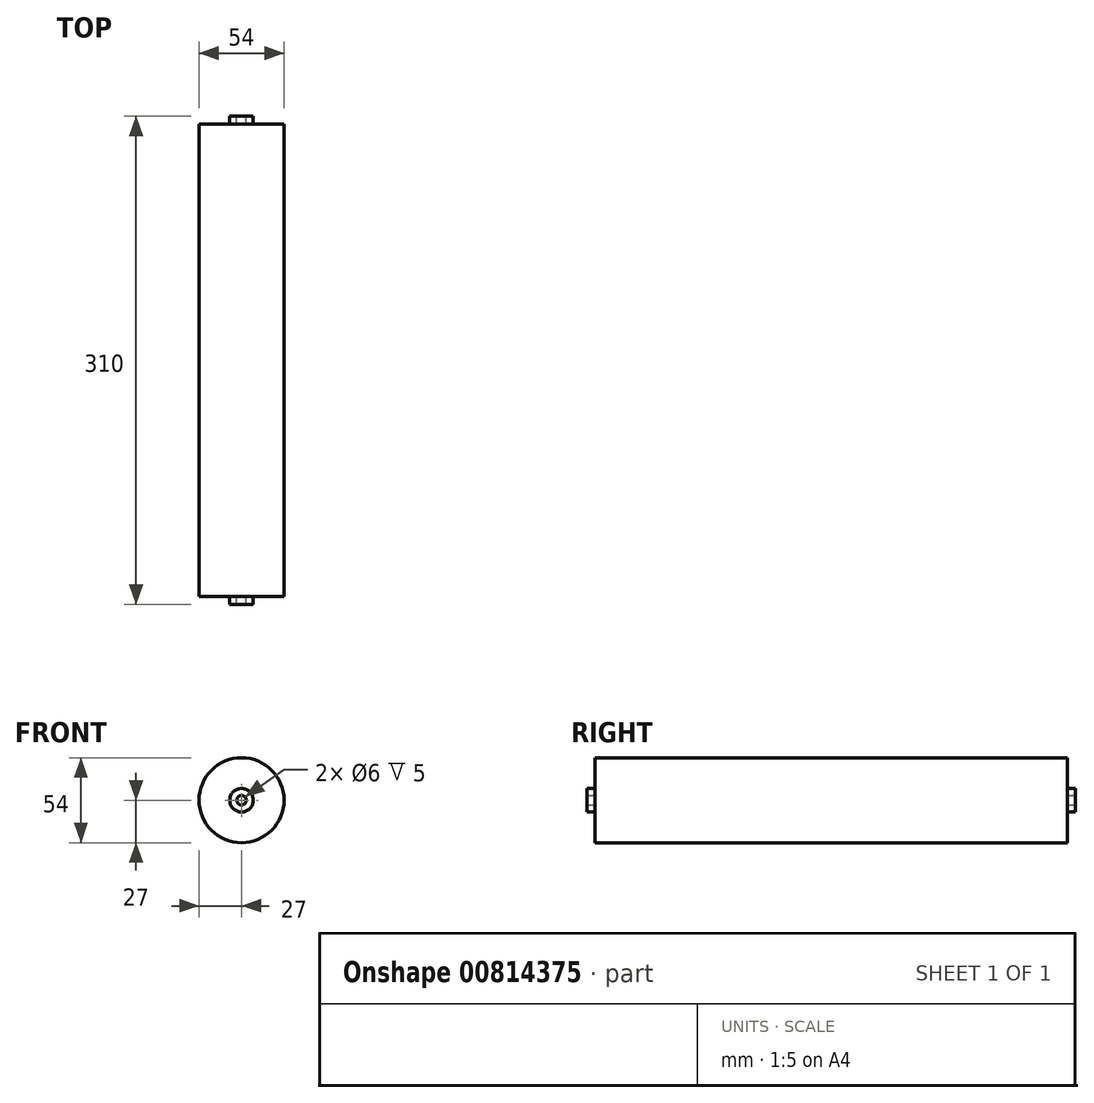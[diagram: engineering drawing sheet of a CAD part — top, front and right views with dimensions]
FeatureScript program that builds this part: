
annotation { "Feature Type Name" : "Feature", "Feature Type Description" : "" }
export const myFeature = defineFeature(function(context is Context, id is Id, definition is map)
    precondition{}
    {
        {
            var Q0;
            Q0=qCreatedBy(makeId("Front.planeOp"),FACE);
            var sketch = newSketch(context, id + "F0", { "sketchPlane" : qUnion([Q0])});
            skCircle(sketch, "E0", {"center": v(0, 0) * mm, "radius": 27 * mm});
            skCircle(sketch, "E1", {"center": v(0, 0) * mm, "radius": 3 * mm});
            skCircle(sketch, "E2", {"center": v(0, 0) * mm, "radius": 7.48 * mm});
            skSolve(sketch);
        }
        {
            var Q0;
            Q0=makeQuery(id+"F0.imprint","IMPRINT",FACE,{"disambiguationData":[TD([[makeQuery(id+"F0.imprint","IMPRINT",EDGE,{"derivedFrom":sQuery(id+"F0.wireOp",EDGE,"E1")}),1.0]])]});
            extrude(context, id + "F1", {"entities" : qUnion([Q0]), "depth" : 300 * mm, "offsetDistance" : 25 * mm, "symmetric" : true});
        }
        {
            var Q0;
            Q0=makeQuery(id+"F0.imprint","IMPRINT",FACE,{"disambiguationData":[TD([[makeQuery(id+"F0.imprint","IMPRINT",EDGE,{"derivedFrom":sQuery(id+"F0.wireOp",EDGE,"E1")}),-1.0]])]});
            extrude(context, id + "F2", {"entities" : qUnion([Q0]), "operationType" : NewBodyOperationType.ADD, "depth" : 310 * mm, "offsetDistance" : 25 * mm, "symmetric" : true});
        }
        {
            var Q0;
            Q0=makeQuery(id+"F0.imprint","IMPRINT",FACE,{"disambiguationData":[TD([[makeQuery(id+"F0.imprint","IMPRINT",EDGE,{"derivedFrom":sQuery(id+"F0.wireOp",EDGE,"E0")}),1.0]])]});
            extrude(context, id + "F3", {"entities" : qUnion([Q0]), "operationType" : NewBodyOperationType.ADD, "depth" : 300 * mm, "offsetDistance" : 25 * mm, "symmetric" : true});
        }
    });
